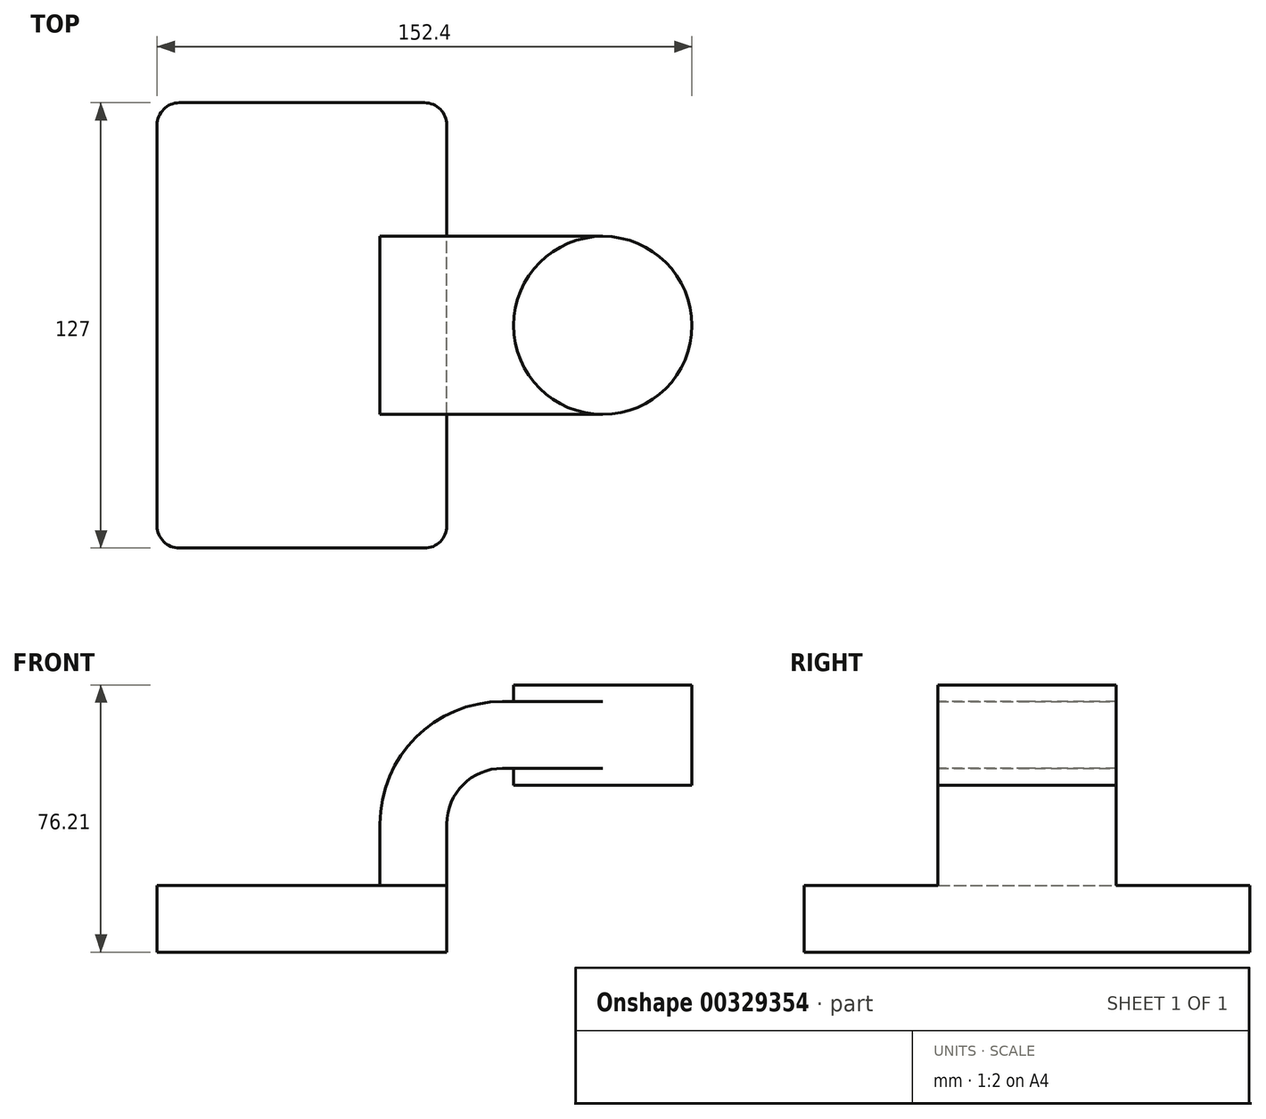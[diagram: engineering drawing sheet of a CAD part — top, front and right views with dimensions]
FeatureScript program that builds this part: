
annotation { "Feature Type Name" : "Feature", "Feature Type Description" : "" }
export const myFeature = defineFeature(function(context is Context, id is Id, definition is map)
    precondition{}
    {
        {
            var Q0;
            Q0=qCreatedBy(makeId("Front.planeOp"),FACE);
            var sketch = newSketch(context, id + "F0", { "sketchPlane" : qUnion([Q0])});
            skLineSegment(sketch, "E0.bottom", {"start": v(41.27, 9.53) * mm, "end": v(-41.28, 9.53) * mm});
            skLineSegment(sketch, "E0.top", {"start": v(41.28, -9.52) * mm, "end": v(-41.27, -9.52) * mm});
            skLineSegment(sketch, "E0.left", {"start": v(41.28, 9.53) * mm, "end": v(41.28, -9.52) * mm});
            skLineSegment(sketch, "E0.right", {"start": v(-41.28, 9.53) * mm, "end": v(-41.27, -9.52) * mm});
            skPoint(sketch, "E0.middle", {"position": v(0, 0) * mm});
            skLineSegment(sketch, "E1.bottom", {"start": v(111.13, 38.1) * mm, "end": v(60.32, 38.1) * mm});
            skLineSegment(sketch, "E1.top", {"start": v(111.13, 66.68) * mm, "end": v(60.33, 66.68) * mm});
            skLineSegment(sketch, "E1.left", {"start": v(111.13, 38.1) * mm, "end": v(111.13, 66.68) * mm});
            skLineSegment(sketch, "E1.right", {"start": v(60.33, 38.1) * mm, "end": v(60.33, 66.68) * mm});
            skPoint(sketch, "E1.middle", {"position": v(85.73, 52.39) * mm});
            skLineSegment(sketch, "E2", {"start": v(41.27, 9.53) * mm, "end": v(41.27, 27) * mm});
            skArc(sketch, "E3", {"start": v(41.27, 27) * mm, "mid": v(45.92, 38.23) * mm, "end": v(57.15, 42.88) * mm});
            skLineSegment(sketch, "E4", {"start": v(57.15, 42.88) * mm, "end": v(85.73, 42.88) * mm});
            skLineSegment(sketch, "E5.0", {"start": v(57.15, 61.93) * mm, "end": v(85.73, 61.93) * mm});
            skArc(sketch, "E5.1", {"start": v(22.23, 27) * mm, "mid": v(32.45, 51.7) * mm, "end": v(57.15, 61.93) * mm});
            skLineSegment(sketch, "E5.2", {"start": v(22.23, 9.53) * mm, "end": v(22.23, 27) * mm});
            skLineSegment(sketch, "E6", {"start": v(85.73, 38.1) * mm, "end": v(85.73, 66.68) * mm});
            skFitSpline(sketch, "E7", {"points": [v(-41.28, 9.53) * mm, v(57.15, 61.93) * mm], "startDerivative": vector(0.14, 95.35) * mm, "endDerivative": vector(139.88, -1.17) * mm});
            skSolve(sketch);
        }
        {
            var Q0;
            Q0=makeQuery(id+"F0.imprint","IMPRINT",FACE,{"disambiguationData":[TD([[makeQuery(id+"F0.imprint","IMPRINT",EDGE,{"derivedFrom":sQuery(id+"F0.wireOp",EDGE,"E0.top")}),-1.0]])]});
            extrude(context, id + "F1", {"entities" : qUnion([Q0]), "endBound" : BoundingType.SYMMETRIC, "depth" : 127 * mm});
        }
        {
            var Q0;
            {var subQ0=sQuery(id+"F0.wireOp",EDGE,"E4");var subQ1=sQuery(id+"F0.wireOp",EDGE,"E1.right");var subQ2=makeQuery(id+"F0.imprint","INTERSECT",VERTEX,{"derivedFrom":[subQ1,subQ0]});Q0=makeQuery(id+"F0.imprint","IMPRINT",FACE,{"disambiguationData":[TD([[makeQuery(id+"F0.imprint","IMPRINT",EDGE,{"disambiguationData":[TD([[subQ2,-1.0]])],"derivedFrom":subQ1}),-1.0]])]});}
            var Q1;
            {var subQ1=sQuery(id+"F0.wireOp",EDGE,"E2");Q1=makeQuery(id+"F0.imprint","IMPRINT",FACE,{"disambiguationData":[TD([[makeQuery(id+"F0.imprint","IMPRINT",EDGE,{"derivedFrom":subQ1}),1.0]])]});}
            extrude(context, id + "F2", {"entities" : qUnion([Q0, Q1]), "operationType" : NewBodyOperationType.ADD, "endBound" : BoundingType.SYMMETRIC, "depth" : 50.8 * mm});
        }
        {
            var Q0;
            Q0=makeQuery(id+"F0.imprint","IMPRINT",FACE,{"disambiguationData":[TD([[makeQuery(id+"F0.imprint","IMPRINT",EDGE,{"derivedFrom":sQuery(id+"F0.wireOp",EDGE,"E5.1")}),1.0]])]});
            extrude(context, id + "F3", {"entities" : qUnion([Q0]), "operationType" : NewBodyOperationType.ADD, "endBound" : BoundingType.SYMMETRIC, "depth" : 15.88 * mm});
        }
        {
            var Q0;
            {var subQ4=sQuery(id+"F0.wireOp",EDGE,"E1.left");Q0=makeQuery(id+"F0.imprint","IMPRINT",FACE,{"disambiguationData":[TD([[makeQuery(id+"F0.imprint","IMPRINT",EDGE,{"derivedFrom":subQ4}),1.0]])]});}
            var Q1;
            Q1=sQuery(id+"F0.wireOp",EDGE,"E6");
            revolve(context, id + "F4", {"operationType" : NewBodyOperationType.ADD, "entities" : qUnion([Q0]), "axis" : qUnion([Q1]), "revolveType" : RevolveType.FULL});
        }
        {
            var Q0;
            Q0=makeQuery(id+"F1.opExtrude","CAP_EDGE",EDGE,{"disambiguationData":[OSD([sQuery(id+"F0.wireOp",EDGE,"E0.left")])],"isStart":false});
            var Q1;
            Q1=makeQuery(id+"F1.opExtrude","CAP_EDGE",EDGE,{"disambiguationData":[OSD([sQuery(id+"F0.wireOp",EDGE,"E0.right")])],"isStart":false});
            var Q2;
            Q2=makeQuery(id+"F1.opExtrude","CAP_EDGE",EDGE,{"disambiguationData":[OSD([sQuery(id+"F0.wireOp",EDGE,"E0.left")])],"isStart":true});
            var Q3;
            Q3=makeQuery(id+"F1.opExtrude","CAP_EDGE",EDGE,{"disambiguationData":[OSD([sQuery(id+"F0.wireOp",EDGE,"E0.right")])],"isStart":true});
            fillet(context, id + "F5", {"entities" : qUnion([Q0, Q1, Q2, Q3]), "radius" : 6.35 * mm, "tangentPropagation" : true, "allowEdgeOverflow" : false});
        }
    });
